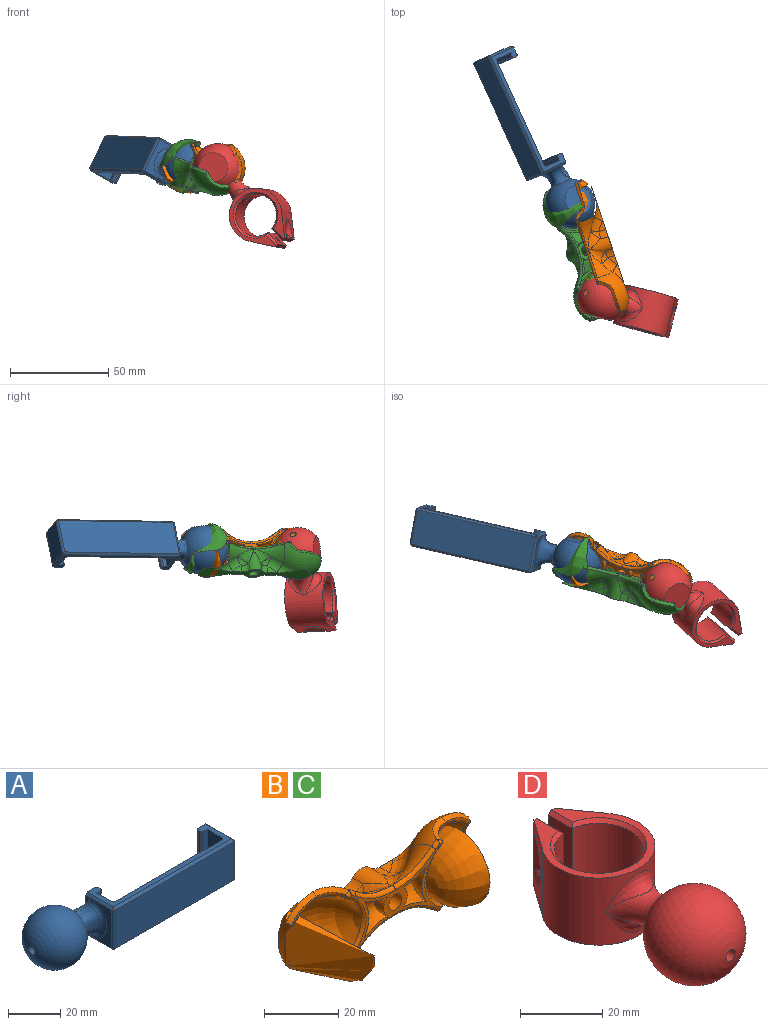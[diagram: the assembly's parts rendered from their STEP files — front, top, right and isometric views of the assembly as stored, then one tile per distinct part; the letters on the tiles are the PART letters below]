
ASSEMBLY  parts=4 mates=4
PART A: 46 faces, bbox 98.6x25.9x25.9 mm
  f0: plane 18.06x11.56mm, normal (-1,0,0), area 79.7mm2, adj f19,f29,f36,f45
  f1: plane 5.66x3.37mm, normal (-1,0,0), area 4.8mm2, adj f8,f20,f45
  f2: sphere r=12.5mm, area 1668.1mm2, adj f3,f18,f19,f20,f21,f22
  f3: plane 15x15mm, normal (0,0,-1), area 176.7mm2, adj f2
  f4: plane 5.66x3.37mm, normal (-1,0,0), area 4.8mm2, adj f8,f21,f36
  f5: plane 20x8mm, normal (1,0,0), area 160mm2, adj f6,f16,f17,f35
  f6: plane 20x2mm, normal (0,-1,0), area 40mm2, adj f5,f16,f17,f27
  f7: plane 20x1mm, normal (1,0,0), area 20mm2, adj f16,f17,f27,f28
  f8: plane 20x5mm, normal (0,1,0), area 99mm2, adj f1,f4,f16,f17,f18,f28,f36,f45
  f9: plane 64x18mm, normal (0,-1,0), area 1152mm2, adj f29,f30,f38,f43
  f10: plane 18x13mm, normal (1,0,0), area 234mm2, adj f30,f31,f40,f41
  f11: plane 20x4mm, normal (0,1,0), area 80mm2, adj f16,f17,f31,f32
  f12: plane 20x1mm, normal (-1,0,0), area 20mm2, adj f16,f17,f32,f33
  f13: plane 20x2mm, normal (0,-1,0), area 40mm2, adj f14,f16,f17,f33
  f14: plane 20x8mm, normal (-1,0,0), area 160mm2, adj f13,f16,f17,f34
  f15: plane 58x20mm, normal (0,1,0), area 1160mm2, adj f16,f17,f34,f35
  f16: plane 64x14mm, normal (0,0,1), area 193.6mm2, adj f5,f6,f7,f8,f11,f12,f13,f14
  f17: plane 64x14mm, normal (0,0,-1), area 193.6mm2, adj f5,f6,f7,f8,f11,f12,f13,f14
  f18: bspline ~14.32x8mm, area 52.9mm2, adj f2,f8,f20,f21
  f19: bspline ~18x13.55mm, area 213.6mm2, adj f0,f2,f20,f21
  f20: bspline ~11.31x8.33mm, area 31.4mm2, adj f1,f2,f18,f19
  f21: bspline ~11.31x8.33mm, area 31.4mm2, adj f2,f4,f18,f19
  f22: cone r=1.62mm half-angle=3deg, axis (-1,0,0), area 33.7mm2, adj f2,f23
  f23: sphere r=9mm, area 804.6mm2, adj f22,f24,f25
  f24: plane 8.83x8.83mm, normal (-1,0,0), area 60.2mm2, adj f23,f26
  f25: plane 12.45x12.45mm, normal (0,0,1), area 121.7mm2, adj f23
  f26: cone r=1.62mm half-angle=3deg, axis (-1,0,0), area 18.7mm2, adj f24
  f27: cylinder r=1mm len=20mm, axis (0,0,1), area 31.4mm2, adj f6,f7,f16,f17
  f28: cylinder r=1mm len=20mm, axis (0,0,-1), area 31.4mm2, adj f7,f8,f16,f17
  f29: cylinder r=1mm len=18mm, axis (0,0,-1), area 28.3mm2, adj f0,f9,f37,f44
  f30: cylinder r=1mm len=18mm, axis (0,0,-1), area 28.3mm2, adj f9,f10,f39,f42
  f31: cylinder r=1mm len=20mm, axis (0,0,-1), area 29.8mm2, adj f10,f11,f40,f41
  f32: cylinder r=1mm len=20mm, axis (0,0,-1), area 31.4mm2, adj f11,f12,f16,f17
  f33: cylinder r=1mm len=20mm, axis (0,0,1), area 31.4mm2, adj f12,f13,f16,f17
  f34: cylinder r=1mm len=20mm, axis (0,0,1), area 31.4mm2, adj f14,f15,f16,f17
  f35: cylinder r=1mm len=20mm, axis (0,0,1), area 31.4mm2, adj f5,f15,f16,f17
  f36: plane 14x1mm, normal (-0.71,0,0.71), area 19.8mm2, adj f0,f4,f8,f16,f37
  f37: cone r=1mm half-angle=45deg, axis (0,0,-1), area 1.1mm2, adj f29,f36,f38
  f38: plane 64x1mm, normal (0,-0.71,0.71), area 90.5mm2, adj f9,f16,f37,f39
  f39: cone r=1mm half-angle=45deg, axis (0,0,-1), area 1.1mm2, adj f30,f38,f40
  f40: plane 14.42x1.42mm, normal (0.71,0,0.71), area 19.5mm2, adj f10,f16,f31,f39
  f41: plane 14.42x1.42mm, normal (0.71,0,-0.71), area 19.5mm2, adj f10,f17,f31,f42
  f42: cone r=1mm half-angle=45deg, axis (0,0,1), area 1.1mm2, adj f30,f41,f43
  f43: plane 64x1mm, normal (0,-0.71,-0.71), area 90.5mm2, adj f9,f17,f42,f44
  f44: cone r=1mm half-angle=45deg, axis (0,0,1), area 1.1mm2, adj f29,f43,f45
  f45: plane 14x1mm, normal (-0.71,0,-0.71), area 19.8mm2, adj f0,f1,f8,f17,f44
PART B: 87 faces, bbox 72.1x19x28.1 mm
  f0: plane 59.78x10.4mm, normal (0,1,0), area 338mm2, adj f1,f2,f7,f13,f14,f15,f19,f21
  f1: plane 4.98x3.76mm, normal (0,0,1), area 10.1mm2, adj f0,f19,f20,f21
  f2: plane 4.98x3.76mm, normal (0,0,-1), area 10.1mm2, adj f0,f24,f25,f26
  f3: revolved ~14.78x8.77mm, area 71.8mm2, adj f7,f24,f26,f28,f42,f77
  f4: plane 9.69x5.17mm, normal (0,-1,0), area 6.9mm2, adj f10,f12,f31,f32,f37
  f5: revolved ~22.89x20.47mm, area 471.5mm2, adj f34,f35,f36,f37,f38,f39
  f6: revolved ~14.78x8.77mm, area 71.8mm2, adj f7,f19,f20,f23,f45,f84
  f7: revolved ~27.88x20.27mm, area 464.7mm2, adj f0,f3,f6,f19,f24,f29,f30,f31
  f8: plane 34.89x21.56mm, normal (0,-1,0), area 123mm2, adj f13,f16,f17,f18,f34,f51,f52,f53
  f9: plane 9.69x5.17mm, normal (0,-1,0), area 6.9mm2, adj f11,f12,f30,f31,f38
  f10: cylinder r=6.5mm len=6.41mm, axis (0,0,1), area 5.7mm2, adj f4,f33,f34,f35,f81
  f11: cylinder r=6.5mm len=6.41mm, axis (0,0,1), area 5.7mm2, adj f9,f29,f34,f36,f75
  f12: cylinder r=9mm len=12.45mm, axis (1,0,0), area 11.1mm2, adj f4,f9,f31,f37,f38,f39
  f13: cylinder r=2.5mm len=13mm, axis (0,1,0), area 204.2mm2, adj f0,f8
  f14: cylinder r=4.5mm len=9.88mm, axis (0,1,0), area 50.1mm2, adj f0,f25,f28,f60,f63
  f15: cylinder r=4.5mm len=9.88mm, axis (0,1,0), area 50.1mm2, adj f0,f21,f23,f56,f58
  f16: revolved ~11.81x5.9mm, area 58.7mm2, adj f8,f17
  f17: revolved ~11.81x8.55mm, area 120.3mm2, adj f8,f16,f18
  f18: cylinder r=4.5mm len=6.32mm, axis (0,1,0), area 17.8mm2, adj f8,f17
  f19: bspline ~12.49x9.13mm, area 25.5mm2, adj f0,f1,f6,f7,f20
  f20: bspline ~9.56x8.32mm, area 36.1mm2, adj f1,f6,f19,f22
  f21: cylinder r=5mm len=3.75mm, axis (0,1,0), area 15.3mm2, adj f0,f1,f15,f22
  f22: sphere r=5mm, area 20.4mm2, adj f20,f21,f23
  f23: bspline ~10.34x8.54mm, area 33.7mm2, adj f6,f15,f22,f58
  f24: bspline ~13.1x9.66mm, area 25.5mm2, adj f0,f2,f3,f7,f26
  f25: cylinder r=5mm len=3.75mm, axis (0,1,0), area 15.3mm2, adj f0,f2,f14,f27
  f26: bspline ~9.56x8.32mm, area 36.1mm2, adj f2,f3,f24,f27
  f27: sphere r=5mm, area 20.4mm2, adj f25,f26,f28
  f28: bspline ~9.38x7.96mm, area 33.7mm2, adj f3,f14,f27,f63
  f29: bspline ~7.76x6.42mm, area 16mm2, adj f7,f11,f30,f75,f76
  f30: bspline ~11.42x7.33mm, area 19.3mm2, adj f7,f9,f29,f31
  f31: bspline ~15.24x4.31mm, area 27mm2, adj f4,f7,f9,f12,f30,f32
  f32: bspline ~11.42x7.33mm, area 19.3mm2, adj f4,f7,f31,f33
  f33: bspline ~7.76x6.42mm, area 16mm2, adj f7,f10,f32,f81,f82
  f34: bspline ~21.95x7.72mm, area 36.2mm2, adj f5,f8,f10,f11,f35,f36,f75,f81
  f35: bspline ~8.5x6.98mm, area 9.1mm2, adj f5,f10,f34,f37
  f36: bspline ~8.5x6.98mm, area 9.1mm2, adj f5,f11,f34,f38
  f37: bspline ~10.93x5.33mm, area 10mm2, adj f4,f5,f12,f35,f39
  f38: bspline ~10.93x5.33mm, area 10mm2, adj f5,f9,f12,f36,f39
  f39: bspline ~14.29x3.88mm, area 9.7mm2, adj f5,f12,f37,f38
  f40: plane 4.98x3.76mm, normal (0,0,1), area 10.1mm2, adj f0,f54,f55,f56
  f41: plane 4.98x3.76mm, normal (0,0,-1), area 10.1mm2, adj f0,f59,f60,f61
  f42: revolved ~14.78x8.77mm, area 71.8mm2, adj f3,f46,f59,f61,f63,f78
  f43: plane 9.69x5.17mm, normal (0,-1,0), area 6.9mm2, adj f48,f50,f66,f67,f72
  f44: revolved ~22.89x20.47mm, area 471.5mm2, adj f69,f70,f71,f72,f73,f74
  f45: revolved ~14.78x8.77mm, area 71.8mm2, adj f6,f46,f54,f55,f58,f86
  f46: revolved ~27.88x20.27mm, area 464.6mm2, adj f0,f42,f45,f54,f59,f64,f65,f66
  f47: plane 9.69x5.17mm, normal (0,-1,0), area 6.9mm2, adj f49,f50,f65,f66,f73
  f48: cylinder r=6.5mm len=6.41mm, axis (0,0,1), area 5.7mm2, adj f43,f68,f69,f70,f83
  f49: cylinder r=6.5mm len=6.41mm, axis (0,0,1), area 5.7mm2, adj f47,f64,f69,f71,f80
  f50: cylinder r=9mm len=12.45mm, axis (-1,0,0), area 11.1mm2, adj f43,f47,f66,f72,f73,f74
  f51: revolved ~11.81x5.9mm, area 58.7mm2, adj f8,f52
  f52: revolved ~11.81x8.55mm, area 120.3mm2, adj f8,f51,f53
  f53: cylinder r=4.5mm len=6.32mm, axis (0,1,0), area 17.8mm2, adj f8,f52
  f54: bspline ~13.1x9.66mm, area 25.5mm2, adj f0,f40,f45,f46,f55
  f55: bspline ~9.56x8.32mm, area 36.1mm2, adj f40,f45,f54,f57
  f56: cylinder r=5mm len=3.75mm, axis (0,1,0), area 15.3mm2, adj f0,f15,f40,f57
  f57: sphere r=5mm, area 16.3mm2, adj f55,f56,f58
  f58: bspline ~10.05x8.54mm, area 33.7mm2, adj f15,f23,f45,f57
  f59: bspline ~12.49x9.13mm, area 25.5mm2, adj f0,f41,f42,f46,f61
  f60: cylinder r=5mm len=3.75mm, axis (0,1,0), area 15.3mm2, adj f0,f14,f41,f62
  f61: bspline ~9.56x8.32mm, area 36.1mm2, adj f41,f42,f59,f62
  f62: sphere r=5mm, area 20.4mm2, adj f60,f61,f63
  f63: bspline ~9.72x7.96mm, area 33.7mm2, adj f14,f28,f42,f62
  f64: bspline ~7.97x7.55mm, area 16mm2, adj f46,f49,f65,f79,f80
  f65: bspline ~11.42x7.33mm, area 19.3mm2, adj f46,f47,f64,f66
  f66: bspline ~15.99x4.66mm, area 27mm2, adj f43,f46,f47,f50,f65,f67
  f67: bspline ~10.29x5.59mm, area 19.3mm2, adj f43,f46,f66,f68
  f68: bspline ~7.76x6.42mm, area 16mm2, adj f46,f48,f67,f83,f85
  f69: bspline ~21.95x7.72mm, area 36.2mm2, adj f8,f44,f48,f49,f70,f71,f80,f83
  f70: bspline ~8.5x6.98mm, area 9.1mm2, adj f44,f48,f69,f72
  f71: bspline ~8.5x6.98mm, area 9.1mm2, adj f44,f49,f69,f73
  f72: bspline ~10.93x5.33mm, area 10mm2, adj f43,f44,f50,f70,f74
  f73: bspline ~10.93x5.33mm, area 10mm2, adj f44,f47,f50,f71,f74
  f74: bspline ~14.29x3.88mm, area 9.7mm2, adj f44,f50,f72,f73
  f75: bspline ~2.26x1.82mm, area 1.9mm2, adj f8,f11,f29,f34,f76
  f76: bspline ~3.63x3.01mm, area 3.6mm2, adj f7,f8,f29,f75,f77
  f77: bspline ~21.28x7mm, area 28.5mm2, adj f3,f7,f8,f76,f78
  f78: bspline ~21.28x7mm, area 28.5mm2, adj f8,f42,f46,f77,f79
  f79: bspline ~3.63x3.01mm, area 3.6mm2, adj f8,f46,f64,f78,f80
  f80: bspline ~2.41x1.9mm, area 1.9mm2, adj f8,f49,f64,f69,f79
  f81: bspline ~2.26x1.82mm, area 1.9mm2, adj f8,f10,f33,f34,f82
  f82: bspline ~3.63x3.01mm, area 3.6mm2, adj f7,f8,f33,f81,f84
  f83: bspline ~2.41x1.9mm, area 1.9mm2, adj f8,f48,f68,f69,f85
  f84: bspline ~21.28x7mm, area 28.5mm2, adj f6,f7,f8,f82,f86
  f85: bspline ~3.63x3.01mm, area 3.6mm2, adj f8,f46,f68,f83,f86
  f86: bspline ~21.28x7mm, area 28.5mm2, adj f8,f45,f46,f84,f85
PART C: same geometry as B
PART D: 34 faces, bbox 27.5x64.3x25 mm
  f0: cylinder r=10.75mm len=21.5mm, axis (0,0,-1), area 1153.3mm2, adj f6,f7,f23,f29,f32
  f1: cylinder r=13.75mm len=27.5mm, axis (0,0,-1), area 1205.2mm2, adj f3,f4,f9,f10,f19,f20
  f2: cylinder r=1.62mm len=3.25mm, axis (1,0,0), area 20.4mm2, adj f7,f13
  f3: plane 20x10.76mm, normal (-0.81,0.58,0), area 162.4mm2, adj f1,f8,f9,f10,f17
  f4: plane 20x10.76mm, normal (0.81,0.58,0), area 162.4mm2, adj f1,f5,f9,f10,f16
  f5: plane 20x2mm, normal (0,1,0), area 39mm2, adj f4,f6,f9,f10,f15,f30,f31
  f6: plane 18x8.11mm, normal (-1,0,0), area 137.6mm2, adj f0,f5,f11,f30,f31
  f7: plane 18x8.11mm, normal (1,0,0), area 137.6mm2, adj f0,f2,f8,f28,f33
  f8: plane 20x2mm, normal (0,1,0), area 39mm2, adj f3,f7,f9,f10,f13,f28,f33
  f9: plane 32.5x27.5mm, normal (0,0,1), area 192.5mm2, adj f1,f3,f4,f5,f8,f31,f32,f33
  f10: plane 32.5x27.5mm, normal (0,0,-1), area 192.5mm2, adj f1,f3,f4,f5,f8,f28,f29,f30
  f11: cylinder r=1.62mm len=3.25mm, axis (1,0,0), area 20.4mm2, adj f6,f15
  f12: cylinder r=3.25mm len=6.27mm, axis (1,0,0), area 0mm2, adj f13,f17
  f13: plane 12x6.75mm, normal (-1,0,0), area 37mm2, adj f2,f8,f12,f17
  f14: cylinder r=3.25mm len=6.27mm, axis (-1,0,0), area 0mm2, adj f15,f16
  f15: plane 12x6.75mm, normal (1,0,0), area 37mm2, adj f5,f11,f14,f16
  f16: bspline ~12.5x8.2mm, area 68.7mm2, adj f4,f14,f15
  f17: bspline ~12.5x8.2mm, area 68.7mm2, adj f3,f12,f13
  f18: revolved ~16.85x16.85mm, area 232.1mm2, adj f19,f20,f21
  f19: bspline ~16.85x8.55mm, area 0mm2, adj f1,f18
  f20: bspline ~16.85x8.55mm, area 0mm2, adj f1,f18
  f21: sphere r=12.5mm, area 1668.1mm2, adj f18,f22,f24
  f22: plane 15x15mm, normal (0,0,-1), area 176.7mm2, adj f21
  f23: cylinder r=1.62mm len=14.5mm, axis (0,-1,0), area 148mm2, adj f0,f26
  f24: cylinder r=1.62mm len=3.54mm, axis (0,-1,0), area 36.2mm2, adj f21,f25
  f25: sphere r=9mm, area 802.8mm2, adj f24,f26,f27
  f26: plane 8.83x8.83mm, normal (0,-1,0), area 52.9mm2, adj f23,f25
  f27: plane 12.45x12.45mm, normal (0,0,1), area 121.7mm2, adj f25
  f28: plane 8.14x1.03mm, normal (0.71,0,-0.71), area 10.9mm2, adj f7,f8,f10,f29
  f29: cone r=11.75mm half-angle=45deg, axis (0,0,-1), area 94.3mm2, adj f0,f10,f28,f30
  f30: plane 8.14x1.03mm, normal (-0.71,0,-0.71), area 10.9mm2, adj f5,f6,f10,f29
  f31: plane 8.14x1.03mm, normal (-0.71,0,0.71), area 10.9mm2, adj f5,f6,f9,f32
  f32: cone r=10.75mm half-angle=45deg, axis (0,0,1), area 94.3mm2, adj f0,f9,f31,f33
  f33: plane 8.14x1.03mm, normal (0.71,0,0.71), area 10.9mm2, adj f7,f8,f9,f32
PLACE A rot(axis=(-0.53,-0.83,0.2),164.6deg) t=(-97.18,53.6,-18.49)mm
PLACE B rot(axis=(0.02,0.01,-1),71.4deg) t=(-80.39,9.16,-19.6)mm
PLACE C rot(axis=(-0.77,0.56,-0.32),130.4deg) t=(-78.98,9.62,-18.72)mm
PLACE D rot(axis=(-0.88,-0.22,-0.42),105deg) t=(-49.79,-20.94,-44.4)mm
MATE ball B.f3 <-> D.f21  axis (-0.32,0.95,0.02) through (-71.36,-14.49,-20.15)mm
MATE ball D.f21 <-> C.f3  axis (0.24,0.97,-0.04) through (-71.36,-14.49,-20.15)mm
MATE ball C.f3 <-> A.f2  axis (0.32,-0.95,-0.02) through (-87.53,33.45,-19.04)mm
MATE ball B.f3 <-> A.f2  axis (0.32,-0.95,-0.02) through (-87.53,33.45,-19.04)mm
